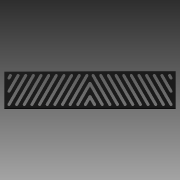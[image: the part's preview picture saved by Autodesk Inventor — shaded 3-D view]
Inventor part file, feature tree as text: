
AUTODESK INVENTOR PART (.ipt)
format: ipt  version: 2014 SP1 (Build 180222100, 222)  size: 479,232 bytes
history: native  units: in
note: dims shown in document units (in); Inventor stores cm internally (conversion verified against a paired STEP export)
features: other x5, sheet_metal_op x4, sketch x4, extrude x1, hole x1, imported_body x1
ambient origin geometry x8: Origin, YZ Plane, XZ Plane, XY Plane, X Axis, Y Axis, Z Axis, Center Point
bodies: Body1 (feature_tree)
feature tree (16):
  other  "PartBody"
  other  "Part11"
  extrude  "Extrusion1"  Depth=0.09in
  sheet_metal_op  "Flange1"
  sheet_metal_op  "Flange2"
  hole  "Hole1"  [1 undecoded]
  imported_body  "Base1"
  sketch  "Sketch1"  dims[d0=0.09in d1=0.045in]
  other  "Plate1"
  sheet_metal_op  "Bend1"
  sketch  "Sketch2"  dims[d2=0.18in d3=0.09in]
  other  "Plate2"
  sheet_metal_op  "Bend2"
  sketch  "Sketch3"  dims[d4=1.18in d5=90.0deg d6=0.09in]
  sketch  "Sketch4"  dims[d7=0.36in d8=0.09in d9=0.09in d10=0.09in d11=0.045in d12=0.18in d13=0.09in d14=1.18in d15=90.0deg d16=0.09in d17=0.36in d18=0.09in d19=0.09in d20=0.5in d21=0.5in d22=11.0236in d24=1.0in d25=0.3937in d27=1.0in d29=0.266in d30=0.75in d31=0.375in d32=0.25in d33=0.5635in d34=0.09in d35=0.8108in d36=0.035in d37=0.035in d38=1.0in d39=0.0in]
  other  "Definition1"
note: 1 required parameter value undecoded (feature->parameter linkage not recoverable at this tier; creation-order binding heuristic only, values carry confidence <= 0.55)
